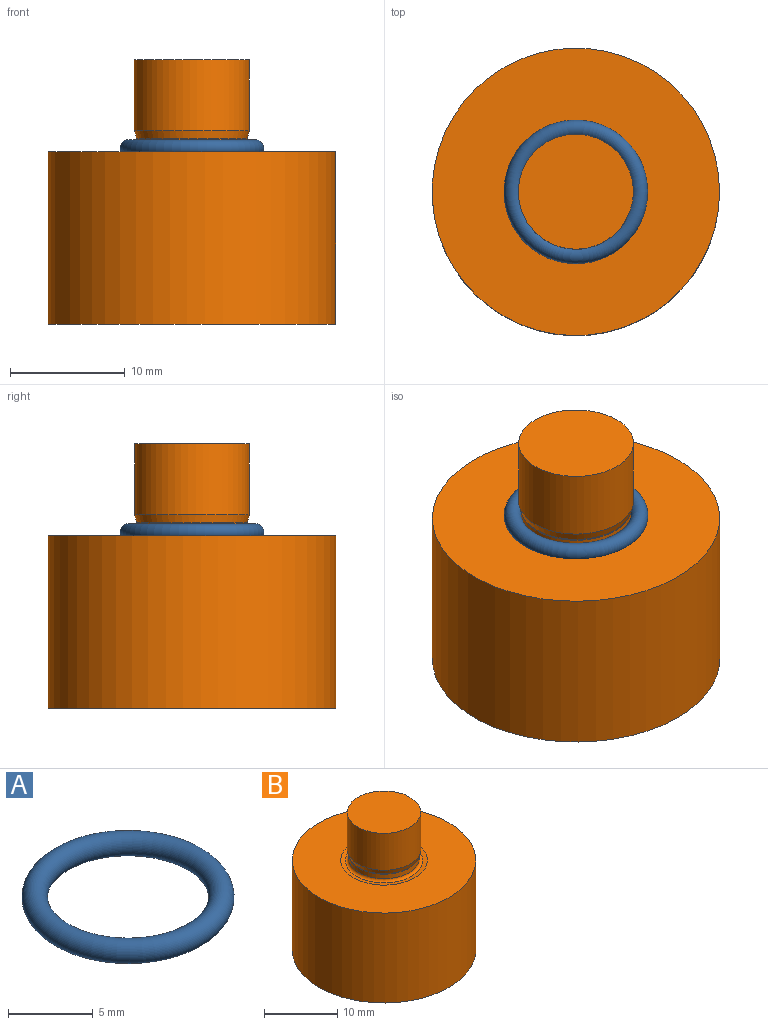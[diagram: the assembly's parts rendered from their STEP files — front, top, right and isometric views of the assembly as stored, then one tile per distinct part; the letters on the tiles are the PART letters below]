
ASSEMBLY  parts=2 mates=1
PART A: 1 faces, bbox 13.5x13.5x1.5 mm
  f0: torus R=5.5mm, axis (0,0,1), area 162.8mm2
PART B: 10 faces, bbox 25x25x23 mm
  f0: cylinder r=5mm len=10mm, axis (0,0,1), area 193.4mm2, adj f1,f9
  f1: cone r=5mm half-angle=15deg, axis (0,0,1), area 22.2mm2, adj f0,f2
  f2: torus R=5.2mm, axis (0,0,1), area 3.2mm2, adj f1,f3
  f3: cylinder r=4.8mm len=9.6mm, axis (0,0,1), area 22.3mm2, adj f2,f4
  f4: torus R=5.2mm, axis (0,0,1), area 21.4mm2, adj f3,f5
  f5: cone r=5.26mm half-angle=82deg, axis (0,0,1), area 22.8mm2, adj f4,f6
  f6: plane 25x25mm, normal (0,0,1), area 381.5mm2, adj f5,f7
  f7: cylinder r=12.5mm len=25mm, axis (0,0,1), area 1178.1mm2, adj f6,f8
  f8: plane 25x25mm, normal (0,0,-1), area 490.9mm2, adj f7
  f9: plane 10x10mm, normal (0,0,1), area 78.5mm2, adj f0
PLACE A t=(0.1,0.04,4.7)mm
PLACE B t=(0.1,0.04,1.12)mm
MATE cylindrical B.f0 <-> A.f0  axis (0,0,1) through (0.1,0.04,4.7)mm
